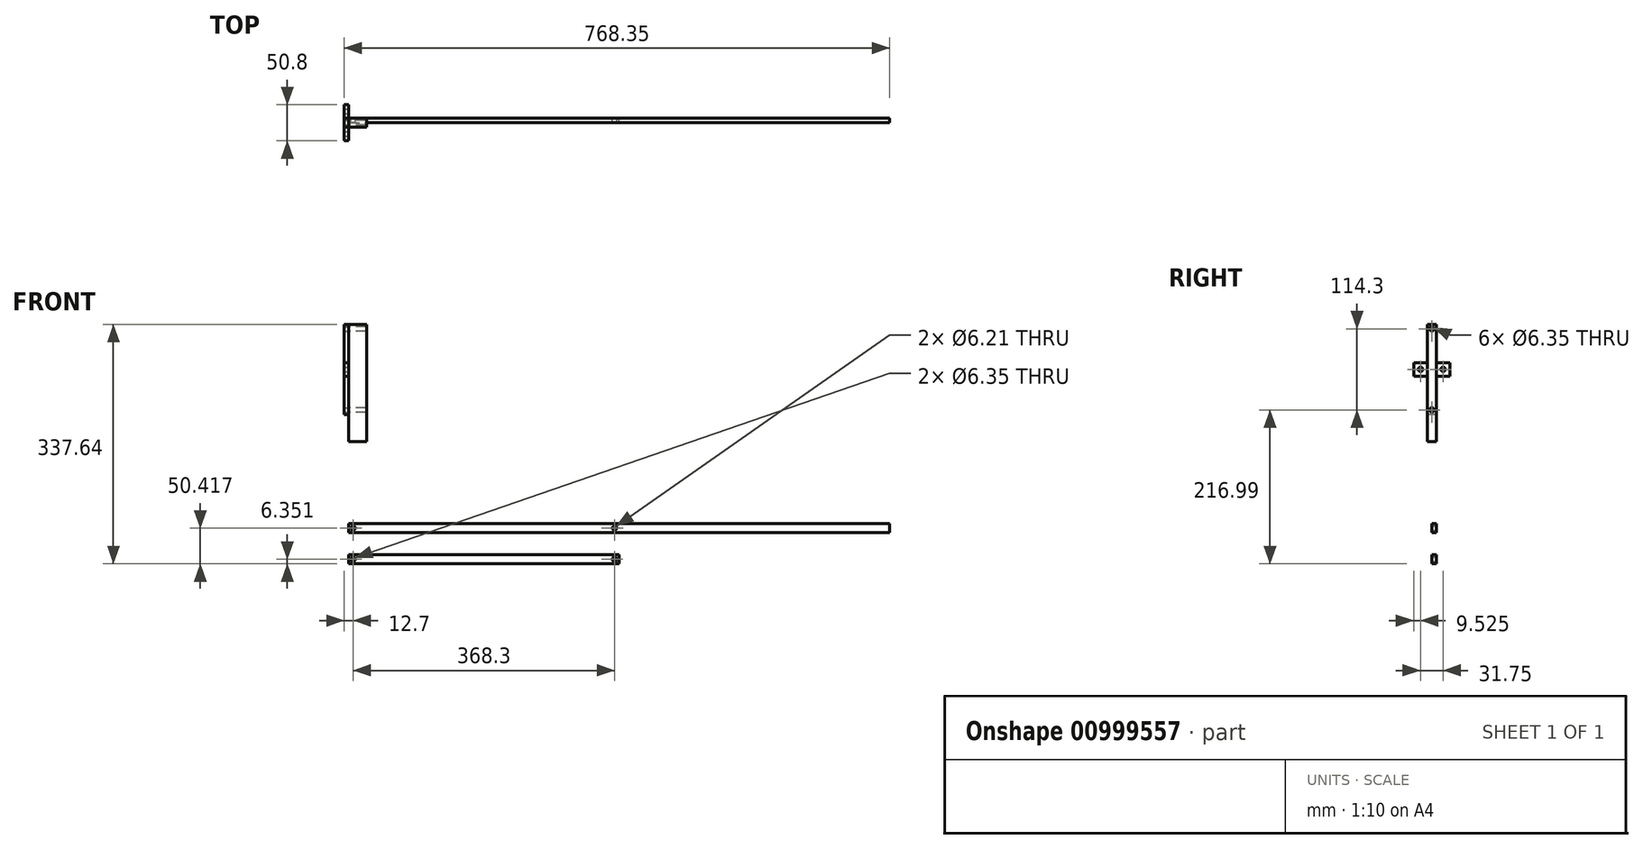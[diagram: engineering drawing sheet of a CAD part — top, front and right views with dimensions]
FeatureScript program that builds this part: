
annotation { "Feature Type Name" : "Feature", "Feature Type Description" : "" }
export const myFeature = defineFeature(function(context is Context, id is Id, definition is map)
    precondition{}
    {
        {
            var Q0;
            Q0=qCreatedBy(makeId("Front.planeOp"),FACE);
            var sketch = newSketch(context, id + "F0", { "sketchPlane" : qUnion([Q0])});
            skLineSegment(sketch, "E0.bottom", {"start": v(0, 0) * mm, "end": v(508, 0) * mm});
            skLineSegment(sketch, "E0.top", {"start": v(0, -38.1) * mm, "end": v(508, -38.1) * mm});
            skLineSegment(sketch, "E0.left", {"start": v(0, 0) * mm, "end": v(0, -38.1) * mm});
            skLineSegment(sketch, "E0.right", {"start": v(508, 0) * mm, "end": v(508, -38.1) * mm});
            skLineSegment(sketch, "E1", {"start": v(0, -19.05) * mm, "end": v(508, -19.05) * mm, "construction": true});
            skCircle(sketch, "E2", {"center": v(254, -19.05) * mm, "radius": 12.7 * mm});
            skLineSegment(sketch, "E3.bottom", {"start": v(0, -38.1) * mm, "end": v(25.4, -38.1) * mm});
            skLineSegment(sketch, "E3.top", {"start": v(0, 127) * mm, "end": v(25.4, 127) * mm});
            skLineSegment(sketch, "E3.left", {"start": v(0, -38.1) * mm, "end": v(0, 127) * mm});
            skLineSegment(sketch, "E3.right", {"start": v(25.4, -38.1) * mm, "end": v(25.4, 127) * mm});
            skLineSegment(sketch, "E4.bottom", {"start": v(0, -153.87) * mm, "end": v(762, -153.87) * mm});
            skLineSegment(sketch, "E4.top", {"start": v(0, -166.57) * mm, "end": v(762, -166.57) * mm});
            skLineSegment(sketch, "E4.left", {"start": v(0, -153.87) * mm, "end": v(0, -166.57) * mm});
            skLineSegment(sketch, "E4.right", {"start": v(762, -153.87) * mm, "end": v(762, -166.57) * mm});
            skLineSegment(sketch, "E5.bottom", {"start": v(0, -197.94) * mm, "end": v(381, -197.94) * mm});
            skLineSegment(sketch, "E5.top", {"start": v(0, -210.64) * mm, "end": v(381, -210.64) * mm});
            skLineSegment(sketch, "E5.left", {"start": v(0, -197.94) * mm, "end": v(0, -210.64) * mm});
            skLineSegment(sketch, "E5.right", {"start": v(381, -197.94) * mm, "end": v(381, -210.64) * mm});
            skLineSegment(sketch, "E6", {"start": v(0, -160.22) * mm, "end": v(762, -160.22) * mm, "construction": true});
            skLineSegment(sketch, "E7", {"start": v(0, -204.29) * mm, "end": v(381, -204.29) * mm, "construction": true});
            skCircle(sketch, "E8", {"center": v(6.35, -204.29) * mm, "radius": 3.18 * mm});
            skCircle(sketch, "E9", {"center": v(6.35, -160.22) * mm, "radius": 3.1 * mm});
            skPoint(sketch, "E10.endSnap0", {"position": v(190.5, -210.64) * mm});
            skLineSegment(sketch, "E11", {"start": v(381, -166.57) * mm, "end": v(381, -153.87) * mm, "construction": true});
            skLineSegment(sketch, "E12", {"start": v(190.5, -210.64) * mm, "end": v(190.5, -197.94) * mm, "construction": true});
            skLineSegment(sketch, "E13", {"start": v(190.5, -197.94) * mm, "end": v(190.5, -153.87) * mm, "construction": true});
            skCircle(sketch, "E14.MirrorC", {"center": v(374.65, -160.22) * mm, "radius": 3.1 * mm});
            skCircle(sketch, "E15.MirrorC", {"center": v(374.65, -204.29) * mm, "radius": 3.18 * mm});
            skSolve(sketch);
        }
        {
            var Q0;
            {var subQ5=sQuery(id+"F0.wireOp",EDGE,"E3.top");Q0=makeQuery(id+"F0.imprint","IMPRINT",FACE,{"disambiguationData":[TD([[makeQuery(id+"F0.imprint","IMPRINT",EDGE,{"derivedFrom":subQ5}),-1.0]])]});}
            var Q1;
            {var subQ5=sQuery(id+"F0.wireOp",EDGE,"E3.bottom");Q1=makeQuery(id+"F0.imprint","IMPRINT",FACE,{"disambiguationData":[TD([[makeQuery(id+"F0.imprint","IMPRINT",EDGE,{"derivedFrom":subQ5}),1.0]])]});}
            var Q2;
            {var subQ1=sQuery(id+"F0.wireOp",EDGE,"E0.top");Q2=makeQuery(id+"F0.imprint","IMPRINT",FACE,{"disambiguationData":[TD([[makeQuery(id+"F0.imprint","IMPRINT",EDGE,{"derivedFrom":subQ1}),1.0]])]});}
            extrude(context, id + "F1", {"entities" : qUnion([Q0, Q1, Q2]), "depth" : 12.7 * mm, "offsetDistance" : 25.4 * mm});
        }
        {
            var Q0;
            Q0=makeQuery(id+"F1.opExtrude","SWEPT_FACE",FACE,{"disambiguationData":[OSD([sQuery(id+"F0.wireOp",EDGE,"E3.left")])]});
            var sketch = newSketch(context, id + "F2", { "sketchPlane" : qUnion([Q0])});
            skLineSegment(sketch, "E16.bottom", {"start": v(0, 127) * mm, "end": v(12.7, 127) * mm});
            skLineSegment(sketch, "E16.top", {"start": v(0, 0) * mm, "end": v(12.7, 0) * mm});
            skLineSegment(sketch, "E16.left", {"start": v(0, 127) * mm, "end": v(0, 0) * mm});
            skLineSegment(sketch, "E16.right", {"start": v(12.7, 127) * mm, "end": v(12.7, 0) * mm});
            skLineSegment(sketch, "E17", {"start": v(6.35, 0) * mm, "end": v(6.35, 127) * mm, "construction": true});
            skCircle(sketch, "E18", {"center": v(6.35, 6.35) * mm, "radius": 3.18 * mm});
            skCircle(sketch, "E19", {"center": v(6.35, 120.65) * mm, "radius": 3.18 * mm});
            skLineSegment(sketch, "E20", {"start": v(0, 63.5) * mm, "end": v(12.7, 63.5) * mm, "construction": true});
            skLineSegment(sketch, "E21.bottom", {"start": v(31.75, 53.98) * mm, "end": v(-19.05, 53.98) * mm});
            skLineSegment(sketch, "E21.top", {"start": v(31.75, 73.03) * mm, "end": v(-19.05, 73.03) * mm});
            skLineSegment(sketch, "E21.left", {"start": v(31.75, 53.98) * mm, "end": v(31.75, 73.03) * mm});
            skLineSegment(sketch, "E21.right", {"start": v(-19.05, 53.98) * mm, "end": v(-19.05, 73.03) * mm});
            skPoint(sketch, "E21.middle", {"position": v(6.35, 63.5) * mm});
            skLineSegment(sketch, "E22", {"start": v(0, 63.5) * mm, "end": v(-19.05, 63.5) * mm, "construction": true});
            skCircle(sketch, "E23", {"center": v(-9.53, 63.5) * mm, "radius": 3.18 * mm});
            skCircle(sketch, "E24.MirrorC", {"center": v(22.23, 63.5) * mm, "radius": 3.18 * mm});
            skSolve(sketch);
        }
        {
            var Q0;
            Q0=makeQuery(id+"F2.imprint","IMPRINT",FACE,{"disambiguationData":[TD([[makeQuery(id+"F2.imprint","IMPRINT",EDGE,{"derivedFrom":sQuery(id+"F2.wireOp",EDGE,"E19")}),1.0]])]});
            var Q1;
            Q1=makeQuery(id+"F2.imprint","IMPRINT",FACE,{"disambiguationData":[TD([[makeQuery(id+"F2.imprint","IMPRINT",EDGE,{"derivedFrom":sQuery(id+"F2.wireOp",EDGE,"E18")}),1.0]])]});
            extrude(context, id + "F3", {"entities" : qUnion([Q0, Q1]), "operationType" : NewBodyOperationType.REMOVE, "oppositeDirection" : true, "depth" : 25.4 * mm, "offsetDistance" : 25.4 * mm});
        }
        {
            var Q0;
            Q0=makeQuery(id+"F2.imprint","IMPRINT",FACE,{"disambiguationData":[TD([[makeQuery(id+"F2.imprint","IMPRINT",EDGE,{"derivedFrom":sQuery(id+"F2.wireOp",EDGE,"E16.bottom")}),1.0]])]});
            var Q1;
            {var subQ5=sQuery(id+"F2.wireOp",EDGE,"E21.right");Q1=makeQuery(id+"F2.imprint","IMPRINT",FACE,{"disambiguationData":[TD([[makeQuery(id+"F2.imprint","IMPRINT",EDGE,{"derivedFrom":subQ5}),-1.0]])]});}
            var Q2;
            {var subQ0=sQuery(id+"F2.wireOp",EDGE,"E21.bottom");var subQ1=sQuery(id+"F2.wireOp",EDGE,"E16.left");var subQ2=makeQuery(id+"F2.imprint","INTERSECT",VERTEX,{"derivedFrom":[subQ1,subQ0]});Q2=makeQuery(id+"F2.imprint","IMPRINT",FACE,{"disambiguationData":[TD([[makeQuery(id+"F2.imprint","IMPRINT",EDGE,{"disambiguationData":[TD([[subQ2,-1.0]])],"derivedFrom":subQ1}),-1.0]])]});}
            var Q3;
            {var subQ5=sQuery(id+"F2.wireOp",EDGE,"E21.left");Q3=makeQuery(id+"F2.imprint","IMPRINT",FACE,{"disambiguationData":[TD([[makeQuery(id+"F2.imprint","IMPRINT",EDGE,{"derivedFrom":subQ5}),1.0]])]});}
            var Q4;
            {var subQ1=sQuery(id+"F2.wireOp",EDGE,"E16.top");Q4=makeQuery(id+"F2.imprint","IMPRINT",FACE,{"disambiguationData":[TD([[makeQuery(id+"F2.imprint","IMPRINT",EDGE,{"derivedFrom":subQ1}),1.0]])]});}
            extrude(context, id + "F4", {"entities" : qUnion([Q0, Q1, Q2, Q3, Q4]), "depth" : 6.35 * mm, "offsetDistance" : 25.4 * mm});
        }
        {
            var Q0;
            Q0=makeQuery(id+"F0.imprint","IMPRINT",FACE,{"disambiguationData":[TD([[makeQuery(id+"F0.imprint","IMPRINT",EDGE,{"derivedFrom":sQuery(id+"F0.wireOp",EDGE,"E4.bottom")}),-1.0]])]});
            var Q1;
            Q1=makeQuery(id+"F0.imprint","IMPRINT",FACE,{"disambiguationData":[TD([[makeQuery(id+"F0.imprint","IMPRINT",EDGE,{"derivedFrom":sQuery(id+"F0.wireOp",EDGE,"E5.bottom")}),-1.0]])]});
            extrude(context, id + "F5", {"entities" : qUnion([Q0, Q1]), "depth" : 6.35 * mm, "offsetDistance" : 25.4 * mm});
        }
    });
